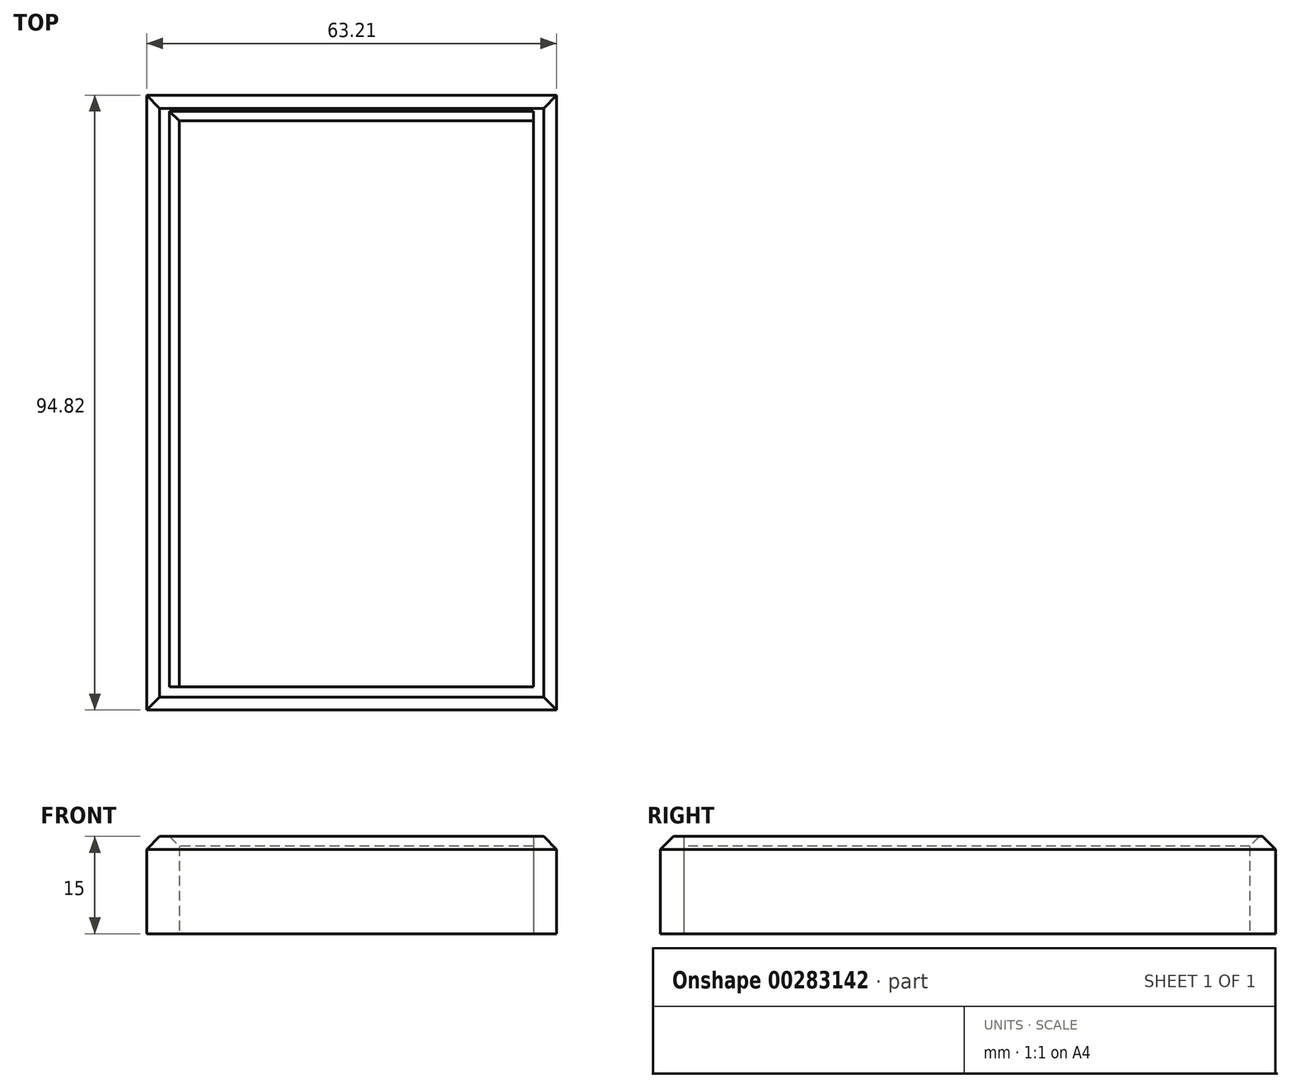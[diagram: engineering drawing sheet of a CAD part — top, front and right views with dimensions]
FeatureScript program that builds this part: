
annotation { "Feature Type Name" : "Feature", "Feature Type Description" : "" }
export const myFeature = defineFeature(function(context is Context, id is Id, definition is map)
    precondition{}
    {
        {
            var Q0;
            Q0=qCreatedBy(makeId("Top.planeOp"),FACE);
            var sketch = newSketch(context, id + "F0", { "sketchPlane" : qUnion([Q0])});
            skLineSegment(sketch, "E0.bottom", {"start": v(-30.48, 40.71) * mm, "end": v(32.73, 40.71) * mm});
            skLineSegment(sketch, "E0.top", {"start": v(-30.48, -54.11) * mm, "end": v(32.73, -54.11) * mm});
            skLineSegment(sketch, "E0.left", {"start": v(-30.48, 40.71) * mm, "end": v(-30.48, -54.11) * mm});
            skLineSegment(sketch, "E0.right", {"start": v(32.73, 40.71) * mm, "end": v(32.73, -54.11) * mm});
            skLineSegment(sketch, "E1.bottom", {"start": v(-25.45, 36.76) * mm, "end": v(29.14, 36.76) * mm});
            skLineSegment(sketch, "E1.top", {"start": v(-25.45, -50.52) * mm, "end": v(29.14, -50.52) * mm});
            skLineSegment(sketch, "E1.left", {"start": v(-25.45, 36.76) * mm, "end": v(-25.45, -50.52) * mm});
            skLineSegment(sketch, "E1.right", {"start": v(29.14, 36.76) * mm, "end": v(29.14, -50.52) * mm});
            skSolve(sketch);
        }
        {
            var Q0;
            Q0=makeQuery(id+"F0.imprint","IMPRINT",FACE,{"disambiguationData":[TD([[makeQuery(id+"F0.imprint","IMPRINT",EDGE,{"derivedFrom":sQuery(id+"F0.wireOp",EDGE,"E0.bottom")}),-1.0]])]});
            extrude(context, id + "F1", {"entities" : qUnion([Q0]), "depth" : 15 * mm});
        }
        {
            var Q0;
            Q0=makeQuery(id+"F1.opExtrude","CAP_EDGE",EDGE,{"disambiguationData":[OSD([sQuery(id+"F0.wireOp",EDGE,"E0.left")])],"isStart":false});
            var Q1;
            Q1=makeQuery(id+"F1.opExtrude","CAP_EDGE",EDGE,{"disambiguationData":[OSD([sQuery(id+"F0.wireOp",EDGE,"E0.bottom")])],"isStart":false});
            var Q2;
            Q2=makeQuery(id+"F1.opExtrude","CAP_EDGE",EDGE,{"disambiguationData":[OSD([sQuery(id+"F0.wireOp",EDGE,"E0.right")])],"isStart":false});
            var Q3;
            Q3=makeQuery(id+"F1.opExtrude","CAP_EDGE",EDGE,{"disambiguationData":[OSD([sQuery(id+"F0.wireOp",EDGE,"E0.top")])],"isStart":false});
            chamfer(context, id + "F2", {"entities" : qUnion([Q0, Q1, Q2, Q3]), "width" : 2 * mm, "tangentPropagation" : true});
        }
        {
            var Q0;
            Q0=makeQuery(id+"F1.opExtrude","CAP_EDGE",EDGE,{"disambiguationData":[OSD([sQuery(id+"F0.wireOp",EDGE,"E1.bottom")])],"isStart":false});
            var Q1;
            Q1=makeQuery(id+"F1.opExtrude","CAP_EDGE",EDGE,{"disambiguationData":[OSD([sQuery(id+"F0.wireOp",EDGE,"E1.left")])],"isStart":false});
            chamfer(context, id + "F3", {"entities" : qUnion([Q0, Q1]), "width" : 1.5 * mm, "tangentPropagation" : true});
        }
    });
